# Revit family: OPTIMA_Compact_Plus_MM_DN32_5,5_RFA_2018
name_source: partatom
category: Pipe Accessories
revit_build: Autodesk Revit LT 2018 (Build: 20180329_1100(x64)
units: mm (PartAtom-declared; Revit-internal decimal feet)

## family parameters
Always vertical = Yes
Cut with Voids When Loaded = No
Part Type = Valve - Breaks Into
Round Connector Dimension = Use Diameter
Shared = No
Work Plane-Based = No

## types (8) — shared parameters
A = 30.00°
Description = Tlakově nezávislý 2-cestný regulační vyvažovací ventil (PICV)
H4 = 12 mm  [stored 0.0393701 ft]
L2D = 104 mm
L2D_Min = 3048 mm
Manufacturer = Hydronic Systems Prague s.r.o.
PLG0 = Yes
QmdConnectorList = 301;D;302;D
R5 = 5 mm  [stored 0.0164042 ft]
R6 = 12 mm  [stored 0.0393701 ft]
R7 = 17 mm  [stored 0.0557743 ft]
R8 = 14 mm  [stored 0.0459318 ft]
R9 = 8 mm  [stored 0.0262467 ft]
Type Comments = vnější závit; PN25; 0~120°C, s měřením
URL = www.hydronic.cz
W2D = 32 mm  [stored 0.104987 ft]
magiPartTypeId = 304
magiProductFamilyId = 3f7bf62c6d3e4202b9bf465282540d

## per-type parameters (varying)
| type | D | H1 | H2 | H3 | H5 | H6 | H6__ve | L1 | L1__ve | L2 | L3 | LL | MC Product Code | R1 | R2 | R3 | R4 | X | Z | magiProductId |
| OPTIMA Compact Plus DN32 M-M 5.5mm | 32 mm | 46 mm  [stored 0.150919 ft] | 10 mm  [stored 0.0328084 ft] | 16 mm  [stored 0.0524934 ft] | 20 mm  [stored 0.0656168 ft] | 66 mm | -66 mm  [stored -0.216535 ft] | 12 mm  [stored 0.0393701 ft] | -12 mm  [stored -0.0393701 ft] | 79 mm | 13 mm  [stored 0.0426509 ft] | 52 mm  [stored 0.170604 ft] | 53-1333  (6/4" M-M; 5.5mm; Qmin-dpmin 550l/h-17.9kPa; Qmax-dpmin 4001l/h-28.0kPa; dpmax 800kPa) | 24 mm  [stored 0.0787402 ft] | 22 mm  [stored 0.0721785 ft] | 32 mm  [stored 0.104987 ft] | 29 mm  [stored 0.0951444 ft] | 13 mm  [stored 0.0426509 ft] | 1 mm  [stored 0.00328084 ft] | ffa5e363716249e69711c5a01860df |
| OPTIMA Compact Plus DN15 M-M 2.5mm | 15 mm | 26 mm  [stored 0.0853018 ft] | 8 mm  [stored 0.0262467 ft] | 18 mm  [stored 0.0590551 ft] | 20 mm  [stored 0.0656168 ft] | 55 mm  [stored 0.180446 ft] | -55 mm  [stored -0.180446 ft] | 8 mm  [stored 0.0262467 ft] | -8 mm  [stored -0.0262467 ft] | 49 mm | 11 mm  [stored 0.0360892 ft] | 33 mm | 53-1324  (3/4" M-M; 2.5mm; Qmin-dpmin 100l/h-14.9kPa; Qmax-dpmin 575l/h-18.5kPa; dpmax 800kPa) | 13 mm  [stored 0.0426509 ft] | 12 mm  [stored 0.0393701 ft] | 19 mm  [stored 0.062336 ft] | 19 mm  [stored 0.062336 ft] | 7 mm  [stored 0.0229659 ft] | 0 mm  [stored 0 ft] | 744f5c1a8b784a0caf7e95e8856504 |
| OPTIMA Compact Plus DN15 M-M 5.0mm | 15 mm | 26 mm  [stored 0.0853018 ft] | 8 mm  [stored 0.0262467 ft] | 18 mm  [stored 0.0590551 ft] | 20 mm  [stored 0.0656168 ft] | 55 mm  [stored 0.180446 ft] | -55 mm  [stored -0.180446 ft] | 8 mm  [stored 0.0262467 ft] | -8 mm  [stored -0.0262467 ft] | 49 mm | 11 mm  [stored 0.0360892 ft] | 33 mm | 53-1325  (3/4" M-M; 5.0mm; Qmin-dpmin 220l/h-16.0kPa; Qmax-dpmin 1330l/h-21.6kPa; dpmax 800kPa) | 13 mm  [stored 0.0426509 ft] | 12 mm  [stored 0.0393701 ft] | 19 mm  [stored 0.062336 ft] | 19 mm  [stored 0.062336 ft] | 7 mm  [stored 0.0229659 ft] | 0 mm  [stored 0 ft] | cc68fe6008154c3392e26a3dfeb2d1 |
| OPTIMA Compact Plus DN20 M-M 5.0mm | 20 mm | 26 mm  [stored 0.0853018 ft] | 8 mm  [stored 0.0262467 ft] | 18 mm  [stored 0.0590551 ft] | 20 mm  [stored 0.0656168 ft] | 59 mm | -59 mm | 8 mm  [stored 0.0262467 ft] | -8 mm  [stored -0.0262467 ft] | 53 mm  [stored 0.173885 ft] | 11 mm  [stored 0.0360892 ft] | 35 mm  [stored 0.114829 ft] | 53-1328  (1" M-M; 5.0mm; Qmin-dpmin 220l/h-16.0kPa; Qmax-dpmin 1330l/h-21.6kPa; dpmax 800kPa) | 17 mm  [stored 0.0557743 ft] | 14 mm  [stored 0.0459318 ft] | 19 mm  [stored 0.062336 ft] | 19 mm  [stored 0.062336 ft] | 10 mm  [stored 0.0328084 ft] | 0 mm  [stored 0 ft] | af4b706c92c34122b2cf0a056ee45d |
| OPTIMA Compact Plus DN20 M-M 5.5mm | 20 mm | 26 mm  [stored 0.0853018 ft] | 8 mm  [stored 0.0262467 ft] | 18 mm  [stored 0.0590551 ft] | 20 mm  [stored 0.0656168 ft] | 59 mm | -59 mm | 8 mm  [stored 0.0262467 ft] | -8 mm  [stored -0.0262467 ft] | 53 mm  [stored 0.173885 ft] | 11 mm  [stored 0.0360892 ft] | 35 mm  [stored 0.114829 ft] | 53-1331  (1" M-M; 5.5mm; Qmin-dpmin 300l/h-17.8kPa; Qmax-dpmin 1800l/h-40.0kPa; dpmax 800kPa) | 17 mm  [stored 0.0557743 ft] | 14 mm  [stored 0.0459318 ft] | 19 mm  [stored 0.062336 ft] | 19 mm  [stored 0.062336 ft] | 10 mm  [stored 0.0328084 ft] | 0 mm  [stored 0 ft] | 3e0f5dc7d8ae4d97894bd6f679fd3a |
| OPTIMA Compact Plus DN25 M-M 5.5mm | 25 mm | 43 mm  [stored 0.141076 ft] | 10 mm  [stored 0.0328084 ft] | 16 mm  [stored 0.0524934 ft] | 20 mm  [stored 0.0656168 ft] | 63 mm  [stored 0.206693 ft] | -63 mm  [stored -0.206693 ft] | 12 mm  [stored 0.0393701 ft] | -12 mm  [stored -0.0393701 ft] | 79 mm | 13 mm  [stored 0.0426509 ft] | 52 mm  [stored 0.170604 ft] | 53-1332  (5/4" M-M; 5.5mm; Qmin-dpmin 600l/h-17.3kPa; Qmax-dpmin 3609l/h-23.0kPa; dpmax 800kPa) | 21 mm  [stored 0.0688976 ft] | 19 mm  [stored 0.062336 ft] | 32 mm  [stored 0.104987 ft] | 29 mm  [stored 0.0951444 ft] | 13 mm  [stored 0.0426509 ft] | 0 mm  [stored 0 ft] | 30c02b6104a34c7a9c49bd2b7417bc |
| OPTIMA Compact Plus DN10 M-M 2.5mm | 10 mm | 30 mm  [stored 0.0984252 ft] | 8 mm  [stored 0.0262467 ft] | 18 mm  [stored 0.0590551 ft] | 17 mm  [stored 0.0557743 ft] | 53 mm  [stored 0.173885 ft] | -53 mm  [stored -0.173885 ft] | 8 mm  [stored 0.0262467 ft] | -8 mm  [stored -0.0262467 ft] | 49 mm | 11 mm  [stored 0.0360892 ft] | 33 mm | 53-1320  (1/2" M-M; 2.5mm; Qmin-dpmin 30l/h-14.3kPa; Qmax-dpmin 200l/h-15.8kPa; dpmax 800kPa) | 11 mm  [stored 0.0360892 ft] | 9 mm  [stored 0.0295276 ft] | 19 mm  [stored 0.062336 ft] | 19 mm  [stored 0.062336 ft] | 7 mm  [stored 0.0229659 ft] | 0 mm  [stored 0 ft] | 273b30465bdd4e038d4ed21de5046f |
| OPTIMA Compact Plus DN10 M-M 5.0mm | 10 mm | 30 mm  [stored 0.0984252 ft] | 8 mm  [stored 0.0262467 ft] | 18 mm  [stored 0.0590551 ft] | 17 mm  [stored 0.0557743 ft] | 53 mm  [stored 0.173885 ft] | -53 mm  [stored -0.173885 ft] | 8 mm  [stored 0.0262467 ft] | -8 mm  [stored -0.0262467 ft] | 49 mm | 11 mm  [stored 0.0360892 ft] | 33 mm | 53-1329  (1/2" M-M; 5.0mm; Qmin-dpmin 65l/h-14.6kPa; Qmax-dpmin 370l/h-17.2kPa; dpmax 800kPa) | 11 mm  [stored 0.0360892 ft] | 9 mm  [stored 0.0295276 ft] | 19 mm  [stored 0.062336 ft] | 19 mm  [stored 0.062336 ft] | 7 mm  [stored 0.0229659 ft] | 0 mm  [stored 0 ft] | 05e83065d4b14c0ea9b5a56fcd5d4f |

note: [stored X ft] marks values corroborated as IEEE doubles in the binary element streams (Revit-internal decimal feet)

## geometry (parser evidence)
native form markers: Sweep x1
no freeform markers — native parametric forms only
